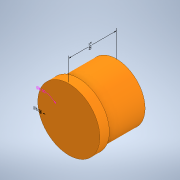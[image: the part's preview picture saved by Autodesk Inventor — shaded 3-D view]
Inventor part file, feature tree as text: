
AUTODESK INVENTOR PART (.ipt)
format: ipt  version: 2021.2 (Build 252289000, 289)  size: 136,704 bytes
history: native  units: in
note: dims shown in document units (in); Inventor stores cm internally (conversion verified against a paired STEP export)
features: extrude x5, sketch x5, other x4
ambient origin geometry x8: Origin, YZ Plane, XZ Plane, XY Plane, X Axis, Y Axis, Z Axis, Center Point
bodies: Solid1 (feature_tree)
feature tree (14):
  other  "Annotations"
  extrude  "Extrusion1"  Depth=5.75in
  extrude  "Extrusion2"  Depth=6.5in
  extrude  "Extrusion3"  Depth=1.0in TaperAngle=0.0deg
  extrude  "Extrusion4"  [1 undecoded]
  extrude  "Extrusion6"  [1 undecoded]
  sketch  "Sketch1"  dims[d2=0.0in d6=5.75in]
  sketch  "Sketch2"  dims[d7=16.0in d8=0.0in d9=6.5in]
  sketch  "Sketch3"  dims[d10=1.0in d11=0.0in d12=1.0in d13=0.0in]
  sketch  "Sketch4"  dims[d19=12.25in d20=0.0in]
  sketch  "Sketch7"  dims[d14=1.3544in d15=6.5in d21=5.0in d3=1.032in d4=6.0in]
  other  "Diameter Dimension 1"
  other  "Diameter Dimension 2"
  other  "Linear Dimension 1"
note: 2 required parameter values undecoded (feature->parameter linkage not recoverable at this tier; creation-order binding heuristic only, values carry confidence <= 0.55)
